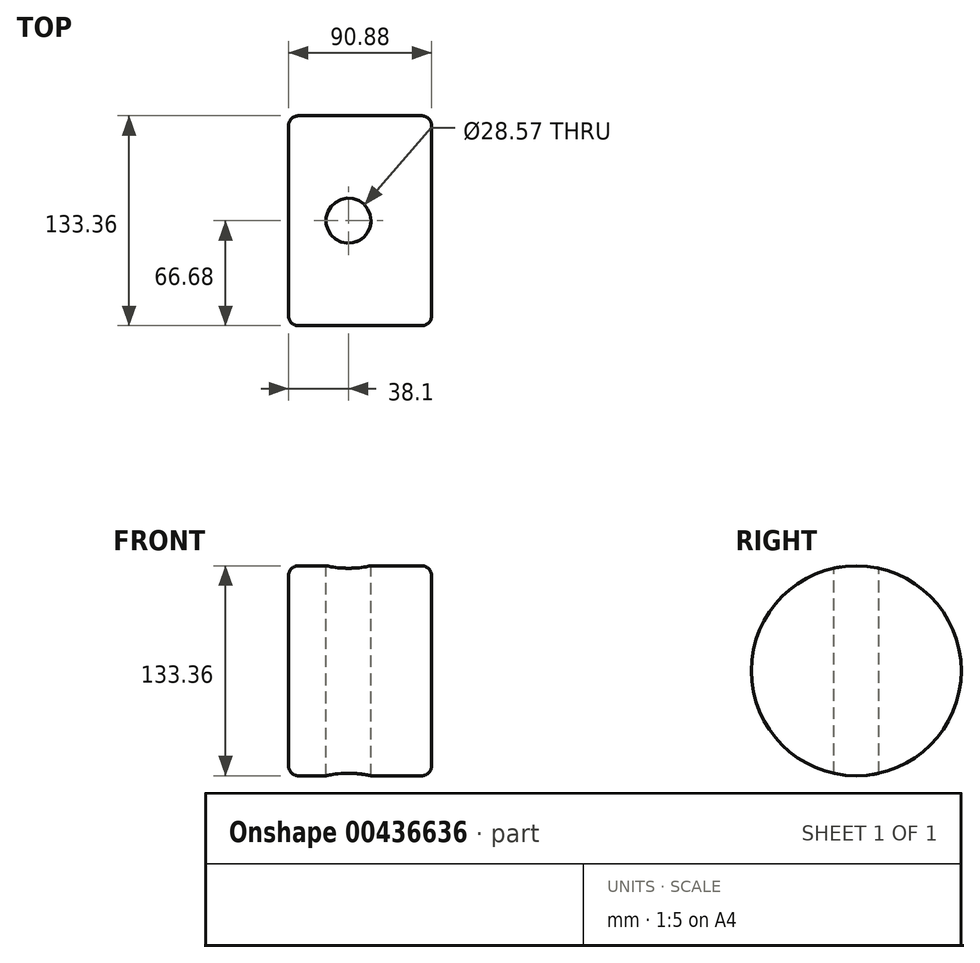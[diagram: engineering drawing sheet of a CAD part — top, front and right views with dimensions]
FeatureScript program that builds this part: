
annotation { "Feature Type Name" : "Feature", "Feature Type Description" : "" }
export const myFeature = defineFeature(function(context is Context, id is Id, definition is map)
    precondition{}
    {
        {
            var Q0;
            Q0=qCreatedBy(makeId("Right.planeOp"),FACE);
            var sketch = newSketch(context, id + "F0", { "sketchPlane" : qUnion([Q0])});
            skCircle(sketch, "E0", {"center": v(0, 0) * mm, "radius": 66.68 * mm});
            skSolve(sketch);
        }
        {
            var Q0;
            Q0 = qSketchRegion(id + "F0", true);
            extrude(context, id + "F1", {"entities" : qUnion([Q0]), "depth" : ((7 * 12) + (6) + (7 / 8)) * mm, "offsetDistance" : 25.4 * mm});
        }
        {
            var Q0;
            Q0=qCreatedBy(makeId("Top.planeOp"),FACE);
            var sketch = newSketch(context, id + "F2", { "sketchPlane" : qUnion([Q0])});
            skLineSegment(sketch, "E1", {"start": v(38.1, 1240.95) * mm, "end": v(38.1, -1338.92) * mm, "construction": true});
            skLineSegment(sketch, "E2", {"start": v(2270.12, 1400.38) * mm, "end": v(2270.12, -1425.88) * mm, "construction": true});
            skCircle(sketch, "E3", {"center": v(38.1, 0) * mm, "radius": 14.29 * mm});
            skCircle(sketch, "E4", {"center": v(2270.12, 0) * mm, "radius": 14.29 * mm});
            skLineSegment(sketch, "E5", {"start": v(0, -0.41) * mm, "end": v(193.23, 0) * mm, "construction": true});
            skSolve(sketch);
        }
        {
            var Q0;
            Q0 = qSketchRegion(id + "F2", true);
            extrude(context, id + "F3", {"entities" : qUnion([Q0]), "operationType" : NewBodyOperationType.REMOVE, "oppositeDirection" : true, "depth" : 152.4 * mm, "offsetDistance" : 25.4 * mm, "symmetric" : true});
        }
        {
            var Q0;
            Q0=makeQuery(id+"F1.opExtrude","CAP_EDGE",EDGE,{"disambiguationData":[OSD([sQuery(id+"F0.wireOp",EDGE,"E0")])],"isStart":true});
            fillet(context, id + "F4", {"entities" : qUnion([Q0]), "tangentPropagation" : true, "radius" : 6.35 * mm, "defaultsChanged" : true, "vertexSettings" : [], "allowEdgeOverflow" : false});
        }
        {
            var Q0;
            Q0=makeQuery(id+"F1.opExtrude","CAP_EDGE",EDGE,{"disambiguationData":[OSD([sQuery(id+"F0.wireOp",EDGE,"E0")])],"isStart":false});
            fillet(context, id + "F5", {"entities" : qUnion([Q0]), "tangentPropagation" : true, "radius" : 6.35 * mm, "defaultsChanged" : true, "vertexSettings" : [], "allowEdgeOverflow" : false});
        }
        {
            var Q0;
            Q0=qCreatedBy(makeId("Right.planeOp"),FACE);
            var sketch = newSketch(context, id + "F6", { "sketchPlane" : qUnion([Q0])});
            skLineSegment(sketch, "E6", {"start": v(0, 0) * mm, "end": v(0, 81.3) * mm, "construction": true});
            skLineSegment(sketch, "E7", {"start": v(-17.46, 85.18) * mm, "end": v(-17.46, 6.77) * mm, "construction": true});
            skLineSegment(sketch, "E8.MirrorCS", {"start": v(17.46, 85.18) * mm, "end": v(17.46, 6.77) * mm, "construction": true});
            skCircle(sketch, "E9", {"center": v(0, 0) * mm, "radius": 66.68 * mm, "construction": true});
            skLineSegment(sketch, "E10", {"start": v(-17.46, 64.35) * mm, "end": v(17.46, 64.35) * mm, "construction": true});
            skLineSegment(sketch, "E11", {"start": v(-31.02, 54.82) * mm, "end": v(28.23, 54.82) * mm, "construction": true});
            skLineSegment(sketch, "E12", {"start": v(-33.44, 77.05) * mm, "end": v(39.68, 77.05) * mm, "construction": true});
            skLineSegment(sketch, "E13", {"start": v(0, 0) * mm, "end": v(-74.6, -43.07) * mm, "construction": true});
            skLineSegment(sketch, "E14.0", {"start": v(-8.74, 15.13) * mm, "end": v(-83.34, -27.94) * mm, "construction": true});
            skLineSegment(sketch, "E15.0", {"start": v(8.74, -15.13) * mm, "end": v(-65.86, -58.2) * mm, "construction": true});
            skLineSegment(sketch, "E16", {"start": v(-64.46, -17.04) * mm, "end": v(-46.99, -47.3) * mm, "construction": true});
            skLineSegment(sketch, "E17.0", {"start": v(-56.21, -12.28) * mm, "end": v(-38.74, -42.54) * mm, "construction": true});
            skLineSegment(sketch, "E18.0", {"start": v(-75.46, -23.39) * mm, "end": v(-57.98, -53.66) * mm, "construction": true});
            skSolve(sketch);
        }
        {
            var Q0;
            Q0=sQuery(id+"F6.wireOp",EDGE,"E11");
            cPoint(context, id + "F7", {"entities" : qUnion([Q0]), "parameter" : 0.5});
        }
        {
            var Q0;
            Q0=qCreatedBy(makeId("Top.planeOp"),FACE);
            var Q1;
            Q1 = qCreatedBy(id + "F7" ,VERTEX);
            cPlane(context, id + "F8", {"entities" : qUnion([Q0, Q1]), "cplaneType" : CPlaneType.PLANE_POINT, "offset" : 25.4 * mm, "width" : 152.4 * mm, "height" : 152.4 * mm});
        }
        {
            var Q0;
            Q0=qCreatedBy(id+"F8.planeOp",FACE);
            var sketch = newSketch(context, id + "F9", { "sketchPlane" : qUnion([Q0])});
            skLineSegment(sketch, "E19", {"start": v(552.45, -0.01) * mm, "end": v(552.45, 0) * mm});
            skLineSegment(sketch, "E20", {"start": v(569.93, 17.46) * mm, "end": v(719.12, 17.46) * mm});
            skLineSegment(sketch, "E21", {"start": v(736.6, 0) * mm, "end": v(736.6, -0.01) * mm});
            skLineSegment(sketch, "E22.MirrorCS", {"start": v(552.45, 0.01) * mm, "end": v(552.45, 0) * mm});
            skLineSegment(sketch, "E23.MirrorCS", {"start": v(569.93, -17.46) * mm, "end": v(719.12, -17.46) * mm});
            skLineSegment(sketch, "E24.MirrorCS", {"start": v(736.6, 0) * mm, "end": v(736.6, 0.01) * mm});
            skLineSegment(sketch, "E25", {"start": v(1670.05, -0.01) * mm, "end": v(1670.05, 0) * mm});
            skLineSegment(sketch, "E26", {"start": v(1687.53, 17.46) * mm, "end": v(1871.65, 17.46) * mm});
            skLineSegment(sketch, "E27", {"start": v(1889.13, 0) * mm, "end": v(1889.13, -0.01) * mm});
            skLineSegment(sketch, "E28.MirrorCS", {"start": v(1670.05, 0.01) * mm, "end": v(1670.05, 0) * mm});
            skLineSegment(sketch, "E29.MirrorCS", {"start": v(1687.53, -17.46) * mm, "end": v(1871.65, -17.46) * mm});
            skLineSegment(sketch, "E30.MirrorCS", {"start": v(1889.13, 0) * mm, "end": v(1889.13, 0.01) * mm});
            skPoint(sketch, "E31.visualSharp", {"position": v(552.45, 17.46) * mm});
            skArc(sketch, "E31.filletArc", {"start": v(569.93, 17.46) * mm, "mid": v(557.57, 12.34) * mm, "end": v(552.45, -0.01) * mm});
            skPoint(sketch, "E32.visualSharp", {"position": v(552.45, -17.46) * mm});
            skArc(sketch, "E32.filletArc", {"start": v(552.45, 0.01) * mm, "mid": v(557.57, -12.34) * mm, "end": v(569.93, -17.46) * mm});
            skPoint(sketch, "E33.visualSharp", {"position": v(736.6, -17.46) * mm});
            skArc(sketch, "E33.filletArc", {"start": v(719.12, -17.46) * mm, "mid": v(731.48, -12.34) * mm, "end": v(736.6, 0.01) * mm});
            skPoint(sketch, "E34.visualSharp", {"position": v(736.6, 17.46) * mm});
            skArc(sketch, "E34.filletArc", {"start": v(736.6, -0.01) * mm, "mid": v(731.48, 12.34) * mm, "end": v(719.12, 17.46) * mm});
            skPoint(sketch, "E35.visualSharp", {"position": v(1889.12, -17.46) * mm});
            skArc(sketch, "E35.filletArc", {"start": v(1871.65, -17.46) * mm, "mid": v(1884, -12.34) * mm, "end": v(1889.13, 0.01) * mm});
            skPoint(sketch, "E36.visualSharp", {"position": v(1889.13, 17.46) * mm});
            skArc(sketch, "E36.filletArc", {"start": v(1889.13, -0.01) * mm, "mid": v(1884, 12.34) * mm, "end": v(1871.65, 17.46) * mm});
            skPoint(sketch, "E37.visualSharp", {"position": v(1670.05, 17.46) * mm});
            skArc(sketch, "E37.filletArc", {"start": v(1687.53, 17.46) * mm, "mid": v(1675.17, 12.34) * mm, "end": v(1670.05, -0.01) * mm});
            skPoint(sketch, "E38.visualSharp", {"position": v(1670.05, -17.46) * mm});
            skArc(sketch, "E38.filletArc", {"start": v(1670.05, 0.01) * mm, "mid": v(1675.17, -12.34) * mm, "end": v(1687.53, -17.46) * mm});
            skSolve(sketch);
        }
        {
            var Q0;
            Q0 = qSketchRegion(id + "F9", true);
            extrude(context, id + "F10", {"entities" : qUnion([Q0]), "operationType" : NewBodyOperationType.REMOVE, "depth" : 25.4 * mm, "offsetDistance" : 25.4 * mm});
        }
        {
            var Q0;
            Q0=sQuery(id+"F2.wireOp",EDGE,"E5");
            cPlane(context, id + "F11", {"entities" : qUnion([Q0]), "cplaneType" : CPlaneType.LINE_ANGLE, "offset" : 25.4 * mm, "angle" : 30 * degree, "width" : 152.4 * mm, "height" : 152.4 * mm});
        }
        {
            var Q0;
            Q0=qCreatedBy(id+"F11.planeOp",FACE);
            var Q1;
            Q1=sQuery(id+"F6.wireOp",VERTEX,"E17.0.end");
            cPlane(context, id + "F12", {"entities" : qUnion([Q0, Q1]), "cplaneType" : CPlaneType.PLANE_POINT, "offset" : 25.4 * mm, "width" : 152.4 * mm, "height" : 152.4 * mm});
        }
        {
            var Q0;
            Q0=qCreatedBy(id+"F12.planeOp",FACE);
            var sketch = newSketch(context, id + "F13", { "sketchPlane" : qUnion([Q0])});
            skLineSegment(sketch, "E39", {"start": v(-552.35, 0.01) * mm, "end": v(-552.35, -0.01) * mm});
            skLineSegment(sketch, "E40", {"start": v(-736.5, 0.01) * mm, "end": v(-736.5, -0.01) * mm});
            skLineSegment(sketch, "E41", {"start": v(55.2, 0) * mm, "end": v(-1019.2, 0) * mm, "construction": true});
            skLineSegment(sketch, "E42", {"start": v(-569.82, 17.46) * mm, "end": v(-719.02, 17.46) * mm});
            skLineSegment(sketch, "E43", {"start": v(-569.82, -17.46) * mm, "end": v(-719.02, -17.46) * mm});
            skPoint(sketch, "E44.orphan", {"position": v(-552.35, -139.22) * mm});
            skPoint(sketch, "E45.orphan", {"position": v(-736.5, -139.22) * mm});
            skPoint(sketch, "E46.visualSharp", {"position": v(-552.35, 17.46) * mm});
            skArc(sketch, "E46.filletArc", {"start": v(-552.35, -0.01) * mm, "mid": v(-557.47, 12.34) * mm, "end": v(-569.82, 17.46) * mm});
            skPoint(sketch, "E47.visualSharp", {"position": v(-552.35, -17.46) * mm});
            skArc(sketch, "E47.filletArc", {"start": v(-569.82, -17.46) * mm, "mid": v(-557.47, -12.34) * mm, "end": v(-552.35, 0.01) * mm});
            skPoint(sketch, "E48.visualSharp", {"position": v(-736.5, -17.46) * mm});
            skArc(sketch, "E48.filletArc", {"start": v(-736.5, 0.01) * mm, "mid": v(-731.38, -12.34) * mm, "end": v(-719.02, -17.46) * mm});
            skPoint(sketch, "E49.visualSharp", {"position": v(-736.5, 17.46) * mm});
            skArc(sketch, "E49.filletArc", {"start": v(-719.02, 17.46) * mm, "mid": v(-731.38, 12.34) * mm, "end": v(-736.5, -0.01) * mm});
            skLineSegment(sketch, "E50", {"start": v(-1687.43, 17.48) * mm, "end": v(-1871.55, 17.48) * mm});
            skLineSegment(sketch, "E51", {"start": v(-1687.43, -17.45) * mm, "end": v(-1871.55, -17.45) * mm});
            skArc(sketch, "E52.filletArc", {"start": v(-1669.95, 0) * mm, "mid": v(-1675.07, 12.36) * mm, "end": v(-1687.43, 17.48) * mm});
            skArc(sketch, "E53.filletArc", {"start": v(-1687.43, -17.45) * mm, "mid": v(-1675.08, -12.34) * mm, "end": v(-1669.95, 0) * mm});
            skArc(sketch, "E54.filletArc", {"start": v(-1889.03, 0) * mm, "mid": v(-1883.9, -12.34) * mm, "end": v(-1871.55, -17.45) * mm});
            skArc(sketch, "E55.filletArc", {"start": v(-1871.55, 17.48) * mm, "mid": v(-1883.9, 12.36) * mm, "end": v(-1889.03, 0) * mm});
            skSolve(sketch);
        }
        {
            var Q0;
            Q0 = qSketchRegion(id + "F13", true);
            extrude(context, id + "F14", {"entities" : qUnion([Q0]), "operationType" : NewBodyOperationType.REMOVE, "oppositeDirection" : true, "depth" : 25.4 * mm, "offsetDistance" : 25.4 * mm});
        }
    });
